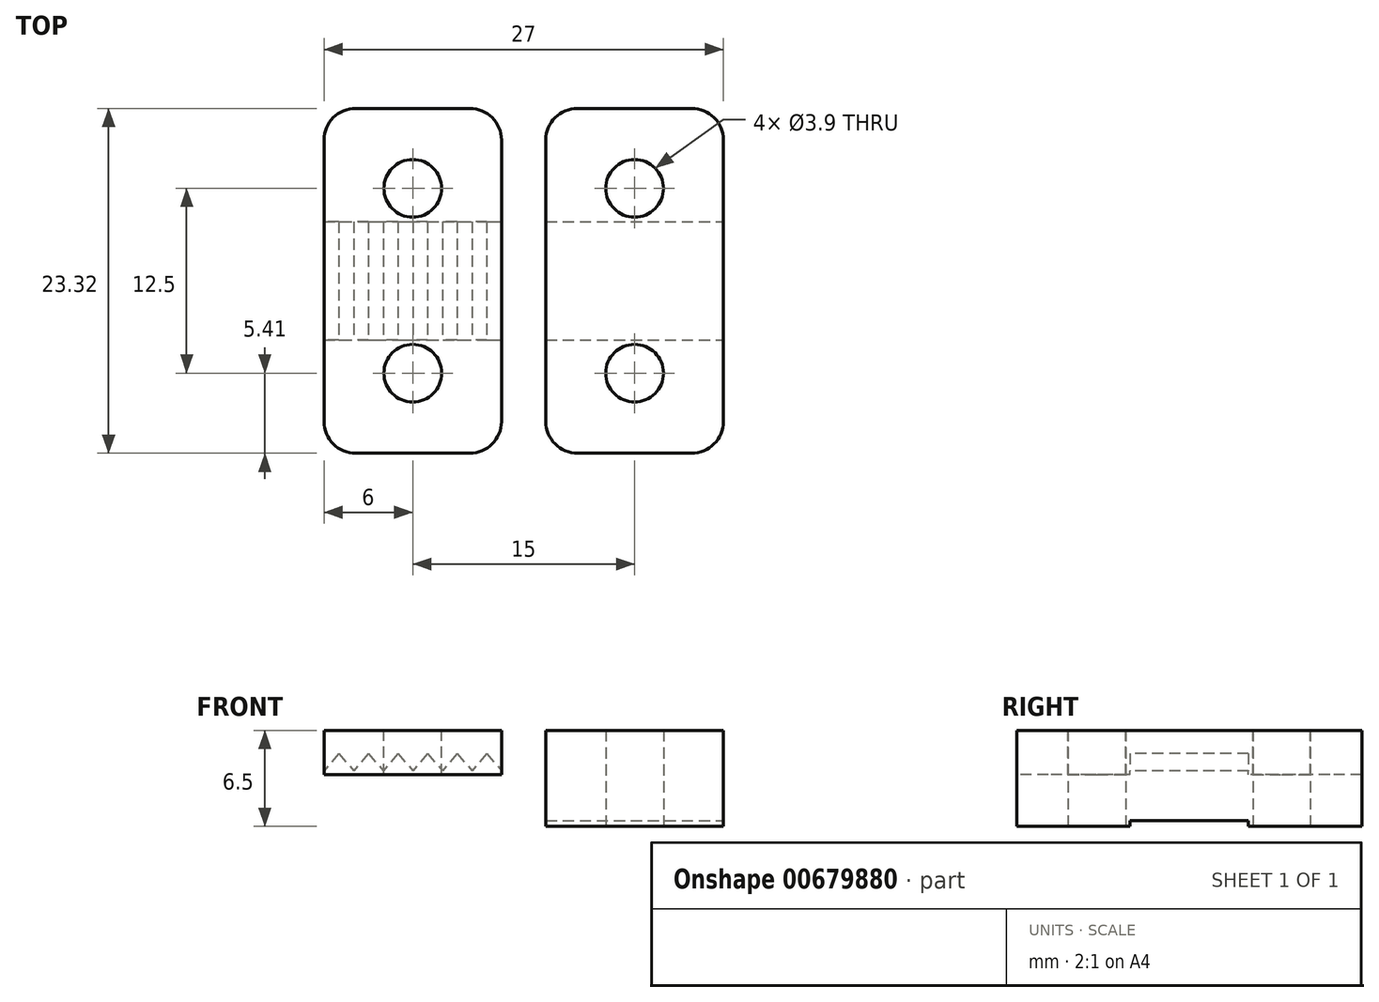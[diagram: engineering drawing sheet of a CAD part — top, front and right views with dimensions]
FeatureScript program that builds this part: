
annotation { "Feature Type Name" : "Feature", "Feature Type Description" : "" }
export const myFeature = defineFeature(function(context is Context, id is Id, definition is map)
    precondition{}
    {
        {
            var Q0;
            Q0=qCreatedBy(makeId("Top.planeOp"),FACE);
            var sketch = newSketch(context, id + "F0", { "sketchPlane" : qUnion([Q0])});
            skCircle(sketch, "E0", {"center": v(0, 6.25) * mm, "radius": 1.95 * mm});
            skLineSegment(sketch, "E1.bottom", {"start": v(-3.85, 11.66) * mm, "end": v(3.85, 11.66) * mm});
            skLineSegment(sketch, "E1.top", {"start": v(-6, 0) * mm, "end": v(6, 0) * mm});
            skLineSegment(sketch, "E1.left", {"start": v(-6, 9.52) * mm, "end": v(-6, 0) * mm});
            skLineSegment(sketch, "E1.right", {"start": v(6, 9.52) * mm, "end": v(6, 0) * mm});
            skPoint(sketch, "E2.visualSharp", {"position": v(-6, 11.66) * mm});
            skArc(sketch, "E2.filletArc", {"start": v(-3.85, 11.66) * mm, "mid": v(-5.37, 11.03) * mm, "end": v(-6, 9.52) * mm});
            skPoint(sketch, "E3.visualSharp", {"position": v(6, 11.66) * mm});
            skArc(sketch, "E3.filletArc", {"start": v(6, 9.52) * mm, "mid": v(5.37, 11.03) * mm, "end": v(3.85, 11.66) * mm});
            skSolve(sketch);
        }
        {
            var Q0;
            Q0=makeQuery(id+"F0.imprint","IMPRINT",FACE,{"disambiguationData":[TD([[makeQuery(id+"F0.imprint","IMPRINT",EDGE,{"derivedFrom":sQuery(id+"F0.wireOp",EDGE,"E0")}),-1.0]])]});
            extrude(context, id + "F1", {"entities" : qUnion([Q0]), "depth" : 6.5 * mm});
        }
        {
            var Q0;
            Q0=makeQuery(id+"F1.opExtrude","SWEPT_BODY",BODY,{"disambiguationData":[OSD([sQuery(id+"F0.wireOp",EDGE,"E0"),sQuery(id+"F0.wireOp",EDGE,"E1.bottom"),sQuery(id+"F0.wireOp",EDGE,"E1.top"),sQuery(id+"F0.wireOp",EDGE,"E1.left"),sQuery(id+"F0.wireOp",EDGE,"E1.right"),sQuery(id+"F0.wireOp",EDGE,"E2.filletArc"),sQuery(id+"F0.wireOp",EDGE,"E3.filletArc")])]});
            var Q1;
            Q1=qCreatedBy(makeId("Front.planeOp"),FACE);
            mirror(context, id + "F2", {"operationType" : NewBodyOperationType.ADD, "entities" : qUnion([Q0]), "mirrorPlane" : qUnion([Q1])});
        }
        {
            var Q0;
            Q0=qCreatedBy(makeId("Top.planeOp"),FACE);
            cPlane(context, id + "F3", {"entities" : qUnion([Q0]), "cplaneType" : CPlaneType.OFFSET, "offset" : 10 * mm, "oppositeDirection" : true, "width" : 150 * mm, "height" : 150 * mm});
        }
        {
            var Q0;
            Q0=qCreatedBy(id+"F3.planeOp",FACE);
            var sketch = newSketch(context, id + "F4", { "sketchPlane" : qUnion([Q0])});
            skCircle(sketch, "E4.0", {"center": v(0, -6.25) * mm, "radius": 1.95 * mm});
            skCircle(sketch, "E5.0", {"center": v(0, 6.25) * mm, "radius": 1.95 * mm});
            skLineSegment(sketch, "E6.0", {"start": v(-6, 9.52) * mm, "end": v(-6, -9.52) * mm});
            skArc(sketch, "E7.0", {"start": v(-3.85, -11.66) * mm, "mid": v(-5.37, -11.03) * mm, "end": v(-6, -9.52) * mm});
            skLineSegment(sketch, "E8.0", {"start": v(-3.85, -11.66) * mm, "end": v(3.85, -11.66) * mm});
            skPoint(sketch, "E9.0", {"position": v(5.37, -11.03) * mm});
            skArc(sketch, "E10.0", {"start": v(6, -9.52) * mm, "mid": v(5.37, -11.03) * mm, "end": v(3.85, -11.66) * mm});
            skLineSegment(sketch, "E11.0", {"start": v(6, 9.52) * mm, "end": v(6, -9.52) * mm});
            skArc(sketch, "E12.0", {"start": v(6, 9.52) * mm, "mid": v(5.37, 11.03) * mm, "end": v(3.85, 11.66) * mm});
            skLineSegment(sketch, "E13.0", {"start": v(-3.85, 11.66) * mm, "end": v(3.85, 11.66) * mm});
            skArc(sketch, "E14.0", {"start": v(-3.85, 11.66) * mm, "mid": v(-5.37, 11.03) * mm, "end": v(-6, 9.52) * mm});
            skSolve(sketch);
        }
        {
            var Q0;
            Q0=makeQuery(id+"F4.imprint","IMPRINT",FACE,{"disambiguationData":[TD([[makeQuery(id+"F4.imprint","IMPRINT",EDGE,{"derivedFrom":sQuery(id+"F4.wireOp",EDGE,"E4.0")}),-1.0]])]});
            extrude(context, id + "F5", {"entities" : qUnion([Q0]), "oppositeDirection" : true, "depth" : 3 * mm});
        }
        {
            var Q0;
            Q0=qCreatedBy(makeId("Front.planeOp"),FACE);
            var sketch = newSketch(context, id + "F6", { "sketchPlane" : qUnion([Q0])});
            skLineSegment(sketch, "E15.0", {"start": v(-6, -13) * mm, "end": v(-6, -12.73) * mm});
            skLineSegment(sketch, "E16.bottom", {"start": v(-6, -13) * mm, "end": v(-4, -13) * mm});
            skLineSegment(sketch, "E16.right", {"start": v(-4, -13) * mm, "end": v(-4, -12.73) * mm});
            skPoint(sketch, "E17", {"position": v(-5, -11.55) * mm});
            skLineSegment(sketch, "E18", {"start": v(-5, -11.55) * mm, "end": v(-4, -12.73) * mm});
            skLineSegment(sketch, "E19", {"start": v(-5, -11.55) * mm, "end": v(-6, -12.73) * mm});
            skPoint(sketch, "E20.orphan", {"position": v(-4, -11.55) * mm});
            skLineSegment(sketch, "E21.trimOffspring", {"start": v(-6, -11.55) * mm, "end": v(-6, -10) * mm});
            skLineSegment(sketch, "E22.1.0.0", {"start": v(-3, -11.55) * mm, "end": v(-2, -12.73) * mm});
            skLineSegment(sketch, "E22.1.0.1", {"start": v(-3, -11.55) * mm, "end": v(-4, -12.73) * mm});
            skLineSegment(sketch, "E22.1.0.3", {"start": v(-4, -13) * mm, "end": v(-2, -13) * mm});
            skLineSegment(sketch, "E22.1.0.4", {"start": v(-2, -13) * mm, "end": v(-2, -12.73) * mm});
            skLineSegment(sketch, "E22.2.0.0", {"start": v(-1, -11.55) * mm, "end": v(0, -12.73) * mm});
            skLineSegment(sketch, "E22.2.0.1", {"start": v(-1, -11.55) * mm, "end": v(-2, -12.73) * mm});
            skLineSegment(sketch, "E22.2.0.2", {"start": v(-2, -13) * mm, "end": v(-2, -12.73) * mm});
            skLineSegment(sketch, "E22.2.0.3", {"start": v(-2, -13) * mm, "end": v(0, -13) * mm});
            skLineSegment(sketch, "E22.2.0.4", {"start": v(0, -13) * mm, "end": v(0, -12.73) * mm});
            skLineSegment(sketch, "E22.3.0.0", {"start": v(1, -11.55) * mm, "end": v(2, -12.73) * mm});
            skLineSegment(sketch, "E22.3.0.1", {"start": v(1, -11.55) * mm, "end": v(0, -12.73) * mm});
            skLineSegment(sketch, "E22.3.0.2", {"start": v(0, -13) * mm, "end": v(0, -12.73) * mm});
            skLineSegment(sketch, "E22.3.0.3", {"start": v(0, -13) * mm, "end": v(2, -13) * mm});
            skLineSegment(sketch, "E22.3.0.4", {"start": v(2, -13) * mm, "end": v(2, -12.73) * mm});
            skLineSegment(sketch, "E22.4.0.0", {"start": v(3, -11.55) * mm, "end": v(4, -12.73) * mm});
            skLineSegment(sketch, "E22.4.0.1", {"start": v(3, -11.55) * mm, "end": v(2, -12.73) * mm});
            skLineSegment(sketch, "E22.4.0.2", {"start": v(2, -13) * mm, "end": v(2, -12.73) * mm});
            skLineSegment(sketch, "E22.4.0.3", {"start": v(2, -13) * mm, "end": v(4, -13) * mm});
            skLineSegment(sketch, "E22.4.0.4", {"start": v(4, -13) * mm, "end": v(4, -12.73) * mm});
            skLineSegment(sketch, "E22.5.0.0", {"start": v(5, -11.55) * mm, "end": v(6, -12.73) * mm});
            skLineSegment(sketch, "E22.5.0.1", {"start": v(5, -11.55) * mm, "end": v(4, -12.73) * mm});
            skLineSegment(sketch, "E22.5.0.2", {"start": v(4, -13) * mm, "end": v(4, -12.73) * mm});
            skLineSegment(sketch, "E22.5.0.3", {"start": v(4, -13) * mm, "end": v(6, -13) * mm});
            skLineSegment(sketch, "E22.5.0.4", {"start": v(6, -13) * mm, "end": v(6, -12.73) * mm});
            skLineSegment(sketch, "E22.direction1", {"start": v(-4, -12.73) * mm, "end": v(-2, -12.73) * mm, "construction": true});
            skSolve(sketch);
        }
        {
            var Q0;
            Q0=qSketchRegion(id+"F6",true);
            extrude(context, id + "F7", {"entities" : qUnion([Q0]), "operationType" : NewBodyOperationType.REMOVE, "oppositeDirection" : true, "depth" : 4 * mm, "hasSecondDirection" : true, "secondDirectionOppositeDirection" : false, "secondDirectionDepth" : 4 * mm});
        }
        {
            var Q0;
            Q0=qCreatedBy(makeId("Top.planeOp"),FACE);
            var sketch = newSketch(context, id + "F8", { "sketchPlane" : qUnion([Q0])});
            skLineSegment(sketch, "E23.0", {"start": v(-6, 9.52) * mm, "end": v(-6, -9.52) * mm});
            skLineSegment(sketch, "E24.0", {"start": v(6, 9.52) * mm, "end": v(6, -9.52) * mm});
            skLineSegment(sketch, "E25.bottom", {"start": v(-6, 4) * mm, "end": v(6, 4) * mm});
            skLineSegment(sketch, "E25.top", {"start": v(-6, 0) * mm, "end": v(6, 0) * mm});
            skLineSegment(sketch, "E25.left", {"start": v(-6, 4) * mm, "end": v(-6, 0) * mm});
            skLineSegment(sketch, "E25.right", {"start": v(6, 4) * mm, "end": v(6, 0) * mm});
            skLineSegment(sketch, "E26.MirrorCS", {"start": v(-6, -4) * mm, "end": v(6, -4) * mm});
            skSolve(sketch);
        }
        {
            var Q0;
            Q0=makeQuery(id+"F8.imprint","IMPRINT",FACE,{"disambiguationData":[TD([[makeQuery(id+"F8.imprint","IMPRINT",EDGE,{"derivedFrom":sQuery(id+"F8.wireOp",EDGE,"E25.bottom")}),-1.0]])]});
            var Q1;
            {var subQ0=sQuery(id+"F8.wireOp",EDGE,"E25.top");Q1=makeQuery(id+"F8.imprint","IMPRINT",FACE,{"disambiguationData":[TD([[makeQuery(id+"F8.imprint","IMPRINT",EDGE,{"derivedFrom":subQ0}),-1.0]])]});}
            extrude(context, id + "F9", {"entities" : qUnion([Q0, Q1]), "operationType" : NewBodyOperationType.REMOVE, "depth" : 0.4 * mm});
        }
        {
            var Q0;
            Q0=makeQuery(id+"F1.opExtrude","SWEPT_BODY",BODY,{"disambiguationData":[OSD([sQuery(id+"F0.wireOp",EDGE,"E0"),sQuery(id+"F0.wireOp",EDGE,"E1.bottom"),sQuery(id+"F0.wireOp",EDGE,"E1.top"),sQuery(id+"F0.wireOp",EDGE,"E1.left"),sQuery(id+"F0.wireOp",EDGE,"E1.right"),sQuery(id+"F0.wireOp",EDGE,"E2.filletArc"),sQuery(id+"F0.wireOp",EDGE,"E3.filletArc")])]});
            var Q1;
            Q1=qCreatedBy(makeId("Right.planeOp"),FACE);
            transform(context, id + "F10", {"entities" : qUnion([Q0]), "transformType" : TransformType.TRANSLATION_DISTANCE, "transformDirection" : qUnion([Q1]), "distance" : 15 * mm, "makeCopy" : false});
        }
        {
            var Q0;
            Q0=makeQuery(id+"F1.opExtrude","SWEPT_BODY",BODY,{"disambiguationData":[OSD([sQuery(id+"F0.wireOp",EDGE,"E0"),sQuery(id+"F0.wireOp",EDGE,"E1.bottom"),sQuery(id+"F0.wireOp",EDGE,"E1.top"),sQuery(id+"F0.wireOp",EDGE,"E1.left"),sQuery(id+"F0.wireOp",EDGE,"E1.right"),sQuery(id+"F0.wireOp",EDGE,"E2.filletArc"),sQuery(id+"F0.wireOp",EDGE,"E3.filletArc")])]});
            var Q1;
            Q1=qCreatedBy(id+"F3.planeOp",FACE);
            transform(context, id + "F11", {"entities" : qUnion([Q0]), "transformType" : TransformType.TRANSLATION_DISTANCE, "transformDirection" : qUnion([Q1]), "distance" : 16.5 * mm, "oppositeDirection" : true, "makeCopy" : false});
        }
    });
